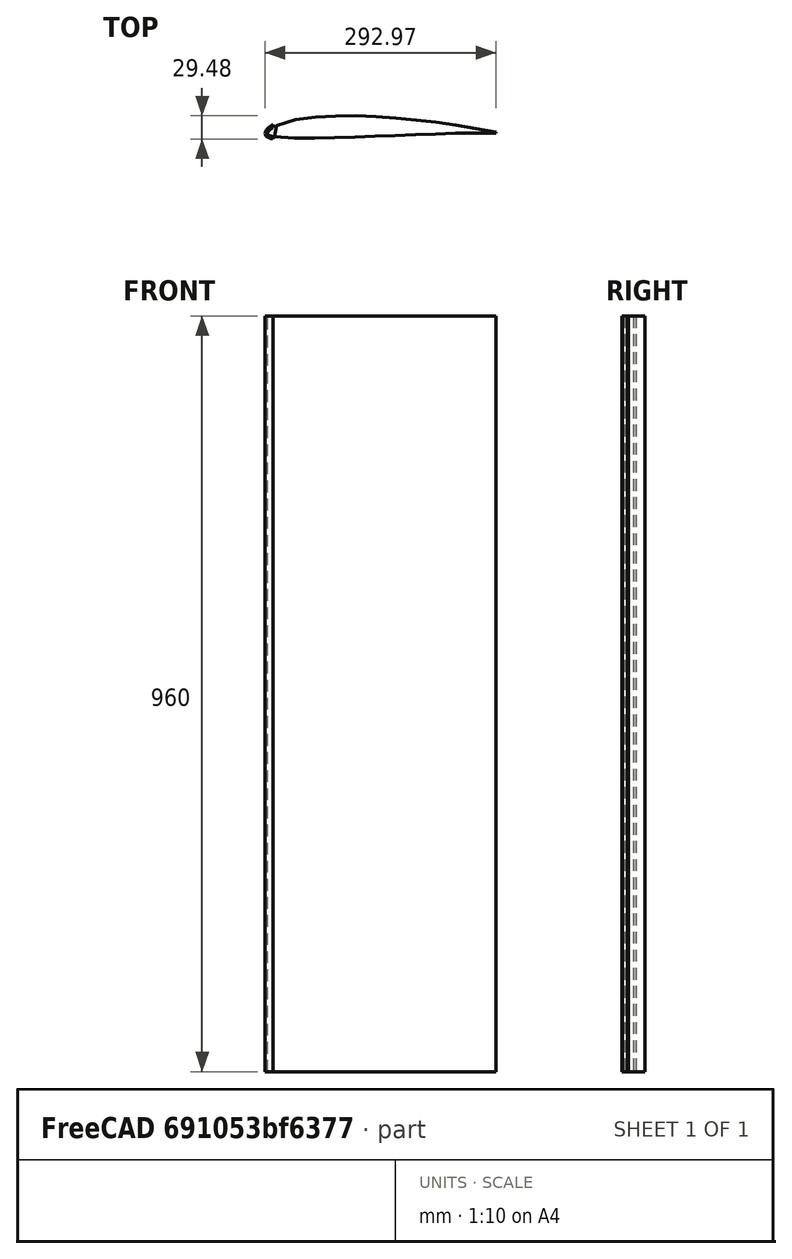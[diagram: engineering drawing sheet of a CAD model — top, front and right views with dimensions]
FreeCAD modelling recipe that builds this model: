
FCSTD DOCUMENT  (FreeCAD 1.0R39319 (Git))
Label: fpv_wing_dummy
License: All rights reserved
LicenseURL: https://en.wikipedia.org/wiki/All_rights_reserved
objects: Sketcher::SketchObject×5, PartDesign::Pocket×3, Part::Part2DObjectPython×2, PartDesign::Plane×2, PartDesign::Pad×2, PartDesign::Body×2, App::DocumentObjectGroup×1, PartDesign::Thickness×1
note: 34 computed .brp shape members not serialized (recipe doc carries the construction recipe); baked Part::Feature solids carry a one-line shape summary decoded from their .brp

FEATURE [Part::Part2DObjectPython] Wire  # Draft 2D object (typed FeaturePython)
  Area = 5447.56
  ChamferSize = 0
  Closed = true
  End = (300,0,0)
  FilletRadius = 0
  Length = 608.938
  MakeFace = true
  Points = (61) [(300,0,0),(299.016,0.126,0),(296.121,0.54,0),(291.438,1.308,0),(285.123,2.433,0),(277.35,3.885,0),(268.275,5.595,0),(258.045,7.47,0),+53 more]
  Start = (300,0,0)
  Subdivisions = 0
FEATURE [App::DocumentObjectGroup] sd7037
  Group = -> [Wire]
FEATURE [Part::Part2DObjectPython] BSpline  # Draft 2D object (typed FeaturePython)
  Area = 5464.75
  Closed = true
  MakeFace = true
  Parameterization = 1
  Points = (60) [(300,0,0),(299.016,0.126,0),(296.121,0.54,0),(291.438,1.308,0),(285.123,2.433,0),(277.35,3.885,0),(268.275,5.595,0),(258.045,7.47,0),+52 more]
FEATURE [PartDesign::Plane] DatumPlane
  AttachmentOffset = pos=(0,0,200) rot=(0,0,1;0rad)
  AttachmentSupport = -> [XY_Plane001]
  Length = 60
  MapMode = 5
  Placement = pos=(0,0,200) rot=(0,0,1;0rad)
  ResizeMode = 0
  Width = 60
FEATURE [Sketcher::SketchObject] Sketch001
  ArcFitTolerance = 1e-06
  AttachmentSupport = -> [DatumPlane]
  FullyConstrained = false
  MakeInternals = false
  MapMode = 5
  Placement = pos=(0,0,200) rot=(0,0,1;0rad)
  sketch-geometry (123):
    g0: BSplineCurve PolesCount=61 KnotsCount=61 Degree=3 IsPeriodic=1
    g1-g61: Circle [constr] x61 (B-spline internal-alignment scaffolding for g0; pole/knot coordinates omitted)
    g62-g122: GeomPoint [constr] x61 (B-spline internal-alignment scaffolding for g0; pole/knot coordinates omitted)
  constraints (123):
    c: InternalAlignment(g1,g0)
    c: Weight(g1) = 1
    c: InternalAlignment(g2,g0)
    c: Equal(g2,g1)
    c: InternalAlignment(g3,g0)
    c: Equal(g3,g1)
    c: InternalAlignment(g4,g0)
    c: Equal(g4,g1)
    c: InternalAlignment(g5,g0)
    c: Equal(g5,g1)
    c: InternalAlignment(g6,g0)
    c: Equal(g6,g1)
    c: InternalAlignment(g7,g0)
    c: Equal(g7,g1)
    c: InternalAlignment(g8,g0)
    c: Equal(g8,g1)
    c: InternalAlignment(g9,g0)
    c: Equal(g9,g1)
    c: InternalAlignment(g10,g0)
    c: Equal(g10,g1)
    c: InternalAlignment(g11,g0)
    c: Equal(g11,g1)
    c: InternalAlignment(g12,g0)
    c: Equal(g12,g1)
    c: InternalAlignment(g13,g0)
    c: Equal(g13,g1)
    c: InternalAlignment(g14,g0)
    c: Equal(g14,g1)
    c: InternalAlignment(g15,g0)
    c: Equal(g15,g1)
    c: InternalAlignment(g16,g0)
    c: Equal(g16,g1)
    c: InternalAlignment(g17,g0)
    c: Equal(g17,g1)
    c: InternalAlignment(g18,g0)
    c: Equal(g18,g1)
    c: InternalAlignment(g19,g0)
    c: Equal(g19,g1)
    c: InternalAlignment(g20,g0)
    c: Equal(g20,g1)
    c: InternalAlignment(g21,g0)
    c: Equal(g21,g1)
    c: InternalAlignment(g22,g0)
    c: Equal(g22,g1)
    c: InternalAlignment(g23,g0)
    c: Equal(g23,g1)
    c: InternalAlignment(g24,g0)
    c: Equal(g24,g1)
    c: InternalAlignment(g25,g0)
    c: Equal(g25,g1)
    c: InternalAlignment(g26,g0)
    c: Equal(g26,g1)
    c: InternalAlignment(g27,g0)
    c: Equal(g27,g1)
    c: InternalAlignment(g28,g0)
    c: Equal(g28,g1)
    c: InternalAlignment(g29,g0)
    c: Equal(g29,g1)
    c: InternalAlignment(g30,g0)
    c: Equal(g30,g1)
    c: InternalAlignment(g31,g0)
    c: Equal(g31,g1)
    c: InternalAlignment(g32,g0)
    c: Equal(g32,g1)
    c: InternalAlignment(g33,g0)
    c: Equal(g33,g1)
    c: InternalAlignment(g34,g0)
    c: Equal(g34,g1)
    c: InternalAlignment(g35,g0)
    c: Equal(g35,g1)
    c: InternalAlignment(g36,g0)
    c: Equal(g36,g1)
    c: InternalAlignment(g37,g0)
    c: Equal(g37,g1)
    c: InternalAlignment(g38,g0)
    c: Equal(g38,g1)
    c: InternalAlignment(g39,g0)
    c: Equal(g39,g1)
    c: InternalAlignment(g40,g0)
    c: Equal(g40,g1)
    c: InternalAlignment(g41,g0)
    c: Equal(g41,g1)
    c: InternalAlignment(g42,g0)
    c: Equal(g42,g1)
    c: InternalAlignment(g43,g0)
    c: Equal(g43,g1)
    c: InternalAlignment(g44,g0)
    c: Equal(g44,g1)
    c: InternalAlignment(g45,g0)
    c: Equal(g45,g1)
    c: InternalAlignment(g46,g0)
    c: Equal(g46,g1)
    c: InternalAlignment(g47,g0)
    c: Equal(g47,g1)
    c: InternalAlignment(g48,g0)
    c: Equal(g48,g1)
    c: InternalAlignment(g49,g0)
    c: Equal(g49,g1)
    c: InternalAlignment(g50,g0)
    c: Equal(g50,g1)
    c: InternalAlignment(g51,g0)
    c: Equal(g51,g1)
    c: InternalAlignment(g52,g0)
    c: Equal(g52,g1)
    c: InternalAlignment(g53,g0)
    c: Equal(g53,g1)
    c: InternalAlignment(g54,g0)
    c: Equal(g54,g1)
    c: InternalAlignment(g55,g0)
    c: Equal(g55,g1)
    c: InternalAlignment(g56,g0)
    c: Equal(g56,g1)
    c: InternalAlignment(g57,g0)
    c: Equal(g57,g1)
    c: InternalAlignment(g58,g0)
    c: Equal(g58,g1)
    c: InternalAlignment(g59,g0)
    c: Equal(g59,g1)
    c: InternalAlignment(g60,g0)
    c: Equal(g60,g1)
    c: InternalAlignment(g61,g0)
    c: Equal(g61,g1)
    c: InternalAlignment(g62-g122 -> g0) x61
FEATURE [PartDesign::Pad] Pad001
  Direction = (0,0,1)
  Length = 960
  Length2 = 10
  Placement = pos=(0,0,200) rot=(0,0,1;0rad)
  Profile = -> Sketch001
  ReferenceAxis = -> Sketch001 [N_Axis]
  Refine = true
  Suppressed = false
  Type = 0
FEATURE [Sketcher::SketchObject] Sketch
  ArcFitTolerance = 1e-06
  AttachmentSupport = -> [XZ_Plane001]
  FullyConstrained = false
  MakeInternals = false
  MapMode = 5
  Placement = pos=(0,0,0) rot=(1,0,0;1.5708rad)
  sketch-geometry (4):
    g0: LineSegment StartX=290 StartY=103.138 StartZ=0 EndX=496.57 EndY=103.138 EndZ=0
    g1: LineSegment StartX=496.57 StartY=103.138 StartZ=0 EndX=496.57 EndY=1315.02 EndZ=0
    g2: LineSegment StartX=496.57 StartY=1315.02 StartZ=0 EndX=290 EndY=1315.02 EndZ=0
    g3: LineSegment StartX=290 StartY=1315.02 StartZ=0 EndX=290 EndY=103.138 EndZ=0
  constraints (9):
    c: Coincident(g0,g1)
    c: Coincident(g1,g2)
    c: Coincident(g2,g3)
    c: Coincident(g3,g0)
    c: Horizontal(g0)
    c: Horizontal(g2)
    c: Vertical(g1)
    c: Vertical(g3)
    c: DistanceX(g-1,g0) = 290
FEATURE [PartDesign::Pocket] Pocket
  BaseFeature = -> Pad001
  Direction = (0,1,-2e-16)
  Length = 100
  Length2 = 5
  Placement = pos=(0,0,200) rot=(0,0,1;0rad)
  Profile = -> Sketch
  ReferenceAxis = -> Sketch [N_Axis]
  Refine = true
  Suppressed = false
  Type = 0
FEATURE [PartDesign::Thickness] Thickness
  Base = -> Pocket [Face4,Face2]
  BaseFeature = -> Pocket
  Intersection = false
  Join = 0
  Mode = 0
  Refine = true
  SupportTransform = false
  Suppressed = false
  Value = 3
FEATURE [Sketcher::SketchObject] Sketch002
  ArcFitTolerance = 1e-06
  AttachmentSupport = -> [Thickness]
  FullyConstrained = false
  MakeInternals = false
  MapMode = 5
  Placement = pos=(0,0,1160) rot=(0,0,1;0rad)
  sketch-geometry (4):
    g0: LineSegment StartX=7 StartY=33.5091 StartZ=0 EndX=7 EndY=-30.0773 EndZ=0
    g1: LineSegment StartX=7 StartY=-30.0773 StartZ=0 EndX=331.752 EndY=-30.0773 EndZ=0
    g2: LineSegment StartX=331.752 StartY=-30.0773 StartZ=0 EndX=331.752 EndY=33.5091 EndZ=0
    g3: LineSegment StartX=331.752 StartY=33.5091 StartZ=0 EndX=7 EndY=33.5091 EndZ=0
  constraints (9):
    c: Coincident(g0,g1)
    c: Coincident(g1,g2)
    c: Coincident(g2,g3)
    c: Coincident(g3,g0)
    c: Vertical(g0)
    c: Vertical(g2)
    c: Horizontal(g1)
    c: Horizontal(g3)
    c: DistanceX(g-1,g0) = 7
FEATURE [PartDesign::Pocket] Pocket001
  BaseFeature = -> Thickness
  Direction = (0,0,-1)
  Length = 1000
  Length2 = 5
  Profile = -> Sketch002
  ReferenceAxis = -> Sketch002 [N_Axis]
  Refine = true
  Suppressed = false
  Type = 0
FEATURE [PartDesign::Body] Body001  label="leading_edge_left"
  AllowCompound = false
  Group = -> [DatumPlane,Sketch001,Pad001,Sketch,Pocket,Thickness,Sketch002,Pocket001]
  Origin = -> Origin001
  Tip = -> Pocket001
FEATURE [PartDesign::Plane] DatumPlane001
  AttachmentOffset = pos=(0,0,200) rot=(0,0,1;0rad)
  AttachmentSupport = -> [XY_Plane002]
  Length = 60
  MapMode = 5
  Placement = pos=(0,0,200) rot=(0,0,1;0rad)
  ResizeMode = 0
  Width = 60
FEATURE [Sketcher::SketchObject] Sketch004
  ArcFitTolerance = 1e-06
  AttachmentSupport = -> [DatumPlane001]
  FullyConstrained = false
  MakeInternals = false
  MapMode = 5
  Placement = pos=(0,0,200) rot=(0,0,1;0rad)
  sketch-geometry (123):
    g0: BSplineCurve PolesCount=61 KnotsCount=61 Degree=3 IsPeriodic=1
    g1-g61: Circle [constr] x61 (B-spline internal-alignment scaffolding for g0; pole/knot coordinates omitted)
    g62-g122: GeomPoint [constr] x61 (B-spline internal-alignment scaffolding for g0; pole/knot coordinates omitted)
  constraints (123):
    c: InternalAlignment(g1,g0)
    c: Weight(g1) = 1
    c: InternalAlignment(g2,g0)
    c: Equal(g2,g1)
    c: InternalAlignment(g3,g0)
    c: Equal(g3,g1)
    c: InternalAlignment(g4,g0)
    c: Equal(g4,g1)
    c: InternalAlignment(g5,g0)
    c: Equal(g5,g1)
    c: InternalAlignment(g6,g0)
    c: Equal(g6,g1)
    c: InternalAlignment(g7,g0)
    c: Equal(g7,g1)
    c: InternalAlignment(g8,g0)
    c: Equal(g8,g1)
    c: InternalAlignment(g9,g0)
    c: Equal(g9,g1)
    c: InternalAlignment(g10,g0)
    c: Equal(g10,g1)
    c: InternalAlignment(g11,g0)
    c: Equal(g11,g1)
    c: InternalAlignment(g12,g0)
    c: Equal(g12,g1)
    c: InternalAlignment(g13,g0)
    c: Equal(g13,g1)
    c: InternalAlignment(g14,g0)
    c: Equal(g14,g1)
    c: InternalAlignment(g15,g0)
    c: Equal(g15,g1)
    c: InternalAlignment(g16,g0)
    c: Equal(g16,g1)
    c: InternalAlignment(g17,g0)
    c: Equal(g17,g1)
    c: InternalAlignment(g18,g0)
    c: Equal(g18,g1)
    c: InternalAlignment(g19,g0)
    c: Equal(g19,g1)
    c: InternalAlignment(g20,g0)
    c: Equal(g20,g1)
    c: InternalAlignment(g21,g0)
    c: Equal(g21,g1)
    c: InternalAlignment(g22,g0)
    c: Equal(g22,g1)
    c: InternalAlignment(g23,g0)
    c: Equal(g23,g1)
    c: InternalAlignment(g24,g0)
    c: Equal(g24,g1)
    c: InternalAlignment(g25,g0)
    c: Equal(g25,g1)
    c: InternalAlignment(g26,g0)
    c: Equal(g26,g1)
    c: InternalAlignment(g27,g0)
    c: Equal(g27,g1)
    c: InternalAlignment(g28,g0)
    c: Equal(g28,g1)
    c: InternalAlignment(g29,g0)
    c: Equal(g29,g1)
    c: InternalAlignment(g30,g0)
    c: Equal(g30,g1)
    c: InternalAlignment(g31,g0)
    c: Equal(g31,g1)
    c: InternalAlignment(g32,g0)
    c: Equal(g32,g1)
    c: InternalAlignment(g33,g0)
    c: Equal(g33,g1)
    c: InternalAlignment(g34,g0)
    c: Equal(g34,g1)
    c: InternalAlignment(g35,g0)
    c: Equal(g35,g1)
    c: InternalAlignment(g36,g0)
    c: Equal(g36,g1)
    c: InternalAlignment(g37,g0)
    c: Equal(g37,g1)
    c: InternalAlignment(g38,g0)
    c: Equal(g38,g1)
    c: InternalAlignment(g39,g0)
    c: Equal(g39,g1)
    c: InternalAlignment(g40,g0)
    c: Equal(g40,g1)
    c: InternalAlignment(g41,g0)
    c: Equal(g41,g1)
    c: InternalAlignment(g42,g0)
    c: Equal(g42,g1)
    c: InternalAlignment(g43,g0)
    c: Equal(g43,g1)
    c: InternalAlignment(g44,g0)
    c: Equal(g44,g1)
    c: InternalAlignment(g45,g0)
    c: Equal(g45,g1)
    c: InternalAlignment(g46,g0)
    c: Equal(g46,g1)
    c: InternalAlignment(g47,g0)
    c: Equal(g47,g1)
    c: InternalAlignment(g48,g0)
    c: Equal(g48,g1)
    c: InternalAlignment(g49,g0)
    c: Equal(g49,g1)
    c: InternalAlignment(g50,g0)
    c: Equal(g50,g1)
    c: InternalAlignment(g51,g0)
    c: Equal(g51,g1)
    c: InternalAlignment(g52,g0)
    c: Equal(g52,g1)
    c: InternalAlignment(g53,g0)
    c: Equal(g53,g1)
    c: InternalAlignment(g54,g0)
    c: Equal(g54,g1)
    c: InternalAlignment(g55,g0)
    c: Equal(g55,g1)
    c: InternalAlignment(g56,g0)
    c: Equal(g56,g1)
    c: InternalAlignment(g57,g0)
    c: Equal(g57,g1)
    c: InternalAlignment(g58,g0)
    c: Equal(g58,g1)
    c: InternalAlignment(g59,g0)
    c: Equal(g59,g1)
    c: InternalAlignment(g60,g0)
    c: Equal(g60,g1)
    c: InternalAlignment(g61,g0)
    c: Equal(g61,g1)
    c: InternalAlignment(g62-g122 -> g0) x61
FEATURE [PartDesign::Pad] Pad002
  Direction = (0,0,1)
  Length = 960
  Length2 = 10
  Placement = pos=(0,0,200) rot=(0,0,1;0rad)
  Profile = -> Sketch004
  ReferenceAxis = -> Sketch004 [N_Axis]
  Refine = true
  Suppressed = false
  Type = 0
FEATURE [Sketcher::SketchObject] Sketch003
  ArcFitTolerance = 1e-06
  AttachmentSupport = -> [XZ_Plane002]
  FullyConstrained = false
  MakeInternals = false
  MapMode = 5
  Placement = pos=(0,0,0) rot=(1,0,0;1.5708rad)
  sketch-geometry (4):
    g0: LineSegment StartX=290 StartY=103.138 StartZ=0 EndX=496.57 EndY=103.138 EndZ=0
    g1: LineSegment StartX=496.57 StartY=103.138 StartZ=0 EndX=496.57 EndY=1315.02 EndZ=0
    g2: LineSegment StartX=496.57 StartY=1315.02 StartZ=0 EndX=290 EndY=1315.02 EndZ=0
    g3: LineSegment StartX=290 StartY=1315.02 StartZ=0 EndX=290 EndY=103.138 EndZ=0
  constraints (9):
    c: Coincident(g0,g1)
    c: Coincident(g1,g2)
    c: Coincident(g2,g3)
    c: Coincident(g3,g0)
    c: Horizontal(g0)
    c: Horizontal(g2)
    c: Vertical(g1)
    c: Vertical(g3)
    c: DistanceX(g-1,g0) = 290
FEATURE [PartDesign::Pocket] Pocket002
  BaseFeature = -> Pad002
  Direction = (0,1,-2e-16)
  Length = 100
  Length2 = 5
  Midplane = true
  Placement = pos=(0,0,200) rot=(0,0,1;0rad)
  Profile = -> Sketch003
  ReferenceAxis = -> Sketch003 [N_Axis]
  Refine = true
  Suppressed = false
  Type = 0
FEATURE [PartDesign::Body] Body002  label="wing_spars_left_inner"
  AllowCompound = false
  Group = -> [DatumPlane001,Sketch004,Pad002,Sketch003,Pocket002]
  Origin = -> Origin002
  Tip = -> Pocket002
